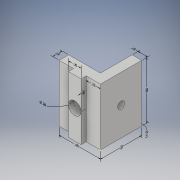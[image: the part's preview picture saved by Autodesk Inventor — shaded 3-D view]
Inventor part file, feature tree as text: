
AUTODESK INVENTOR PART (.ipt)
format: ipt  version: 2018 (Build 220112000, 112)  size: 153,600 bytes
history: native  units: in
note: dims shown in document units (in); Inventor stores cm internally (conversion verified against a paired STEP export)
features: other x11, sketch x5, hole x2, extrude x1
ambient origin geometry x8: Origin, YZ Plane, XZ Plane, XY Plane, X Axis, Y Axis, Z Axis, Center Point
bodies: Solid1 (feature_tree)
feature tree (19):
  other  "Annotations"
  extrude  "Extrusion1"  Depth=0.15in
  sketch  "Sketch2"  dims[d2=0.225in d3=0.2in]
  hole  "Hole2"  [1 undecoded]
  sketch  "Sketch5"  dims[d6=0.15in]
  sketch  "Sketch6"  dims[d7=0.9in d8=0.0in d17=0.325in d18=0.11in d19=0.75in d20=0.25in d21=0.13in d22=0.5635in d23=1.0in d24=0.8108in d46=0.325in d47=0.45in d48=0.2in d49=0.75in d50=0.35in d51=0.22in d52=0.5635in d53=1.0in d54=0.8108in d25=0.2727in d26=0.2095in d27=0.9in d28=0.3012in d29=0.2994in d30=0.65in d31=0.356in d32=0.0293in d33=0.15in d34=0.2979in d35=0.1911in d36=0.15in d37=0.244in d38=0.275in d39=0.65in d40=0.0616in d41=0.058in d42=0.2in d55=0.1689in d56=0.1957in d57=0.08in d58=0.3568in d59=0.3235in d60=0.225in d61=1.4264in d62=0.2491in d63=0.1583in d64=0.2in d65=2.2126in d66=0.0959in d67=0.1533in d68=0.11in d10=1.0in d11=1.0in]
  hole  "Hole3"  [1 undecoded]
  sketch  "Sketch1"  dims[d0=0.65in d1=0.15in]
  sketch  "Sketch4"  dims[d4=0.08in d5=0.65in]
  other  "Linear Dimension 1"
  other  "Linear Dimension 2"
  other  "Linear Dimension 3"
  other  "Linear Dimension 4"
  other  "Linear Dimension 5"
  other  "Linear Dimension 6"
  other  "Linear Dimension 7"
  other  "Linear Dimension 8"
  other  "Diameter Dimension 1"
  other  "Diameter Dimension 2"
note: 2 required parameter values undecoded (feature->parameter linkage not recoverable at this tier; creation-order binding heuristic only, values carry confidence <= 0.55)
